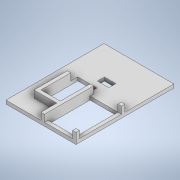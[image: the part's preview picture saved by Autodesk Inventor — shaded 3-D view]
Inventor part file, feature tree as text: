
AUTODESK INVENTOR PART (.ipt)
format: ipt  version: 2022 (Build 260153000, 153)  size: 175,616 bytes
history: native  units: in
note: dims shown in document units (in); Inventor stores cm internally (conversion verified against a paired STEP export)
features: extrude x7, sketch x7
ambient origin geometry x8: Origin, YZ Plane, XZ Plane, XY Plane, X Axis, Y Axis, Z Axis, Center Point
bodies: Solid1 (feature_tree)
feature tree (14):
  extrude  "main plate"  Depth=5.0in
  extrude  "battery standoffs"  Depth=0.25in
  extrude  "breadboard hole"  Depth=2.0in
  extrude  "battery hole"  Depth=0.5in TaperAngle=0.0deg
  extrude  "breadboard standoffs"  Depth=1.875in
  extrude  "wiring hole"  Depth=0.25in TaperAngle=0.0deg
  extrude  "power switch mount"  Depth=0.25in TaperAngle=0.0deg
  sketch  "Sketch1"  dims[d0=7.0in d1=5.0in]
  sketch  "Sketch4"  dims[d2=0.25in d3=0.0in d12=0.25in]
  sketch  "Sketch5"  dims[d13=0.25in d14=2.0in]
  sketch  "Sketch6"  dims[d15=3.0in d16=0.5in d17=0.0in]
  sketch  "Sketch9"  dims[d18=1.375in d19=1.875in]
  sketch  "Sketch10"  dims[d20=0.25in d21=0.0in d22=0.25in d23=0.0in]
  sketch  "Sketch11"  dims[d24=0.5in d25=0.0in d26=0.25in d27=0.0in d28=0.5in d29=0.8125in d30=0.25in d31=0.0in]
